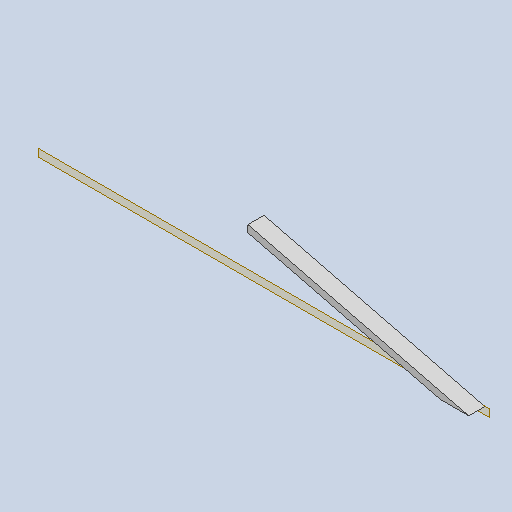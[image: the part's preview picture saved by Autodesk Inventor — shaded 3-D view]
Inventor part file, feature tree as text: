
AUTODESK INVENTOR PART (.ipt)
format: ipt  version: 2025 (Build 290162000, 162)  size: 81,408 bytes
history: native  units: in
note: dims shown in document units (in); Inventor stores cm internally (conversion verified against a paired STEP export)
features: other x3, sketch x1, plane x1
ambient origin geometry x8: Origin, YZ Plane, XZ Plane, XY Plane, X Axis, Y Axis, Z Axis, Center Point
bodies: Solid1 (feature_tree)
feature tree (5):
  other  "top head slant.ipt"
  other  "Solid1::top head slant.ipt"
  other  "TaggingFeature1"
  sketch  "Sketch1"  dims[d0=0.3937in]
  plane  "Work Plane1"
